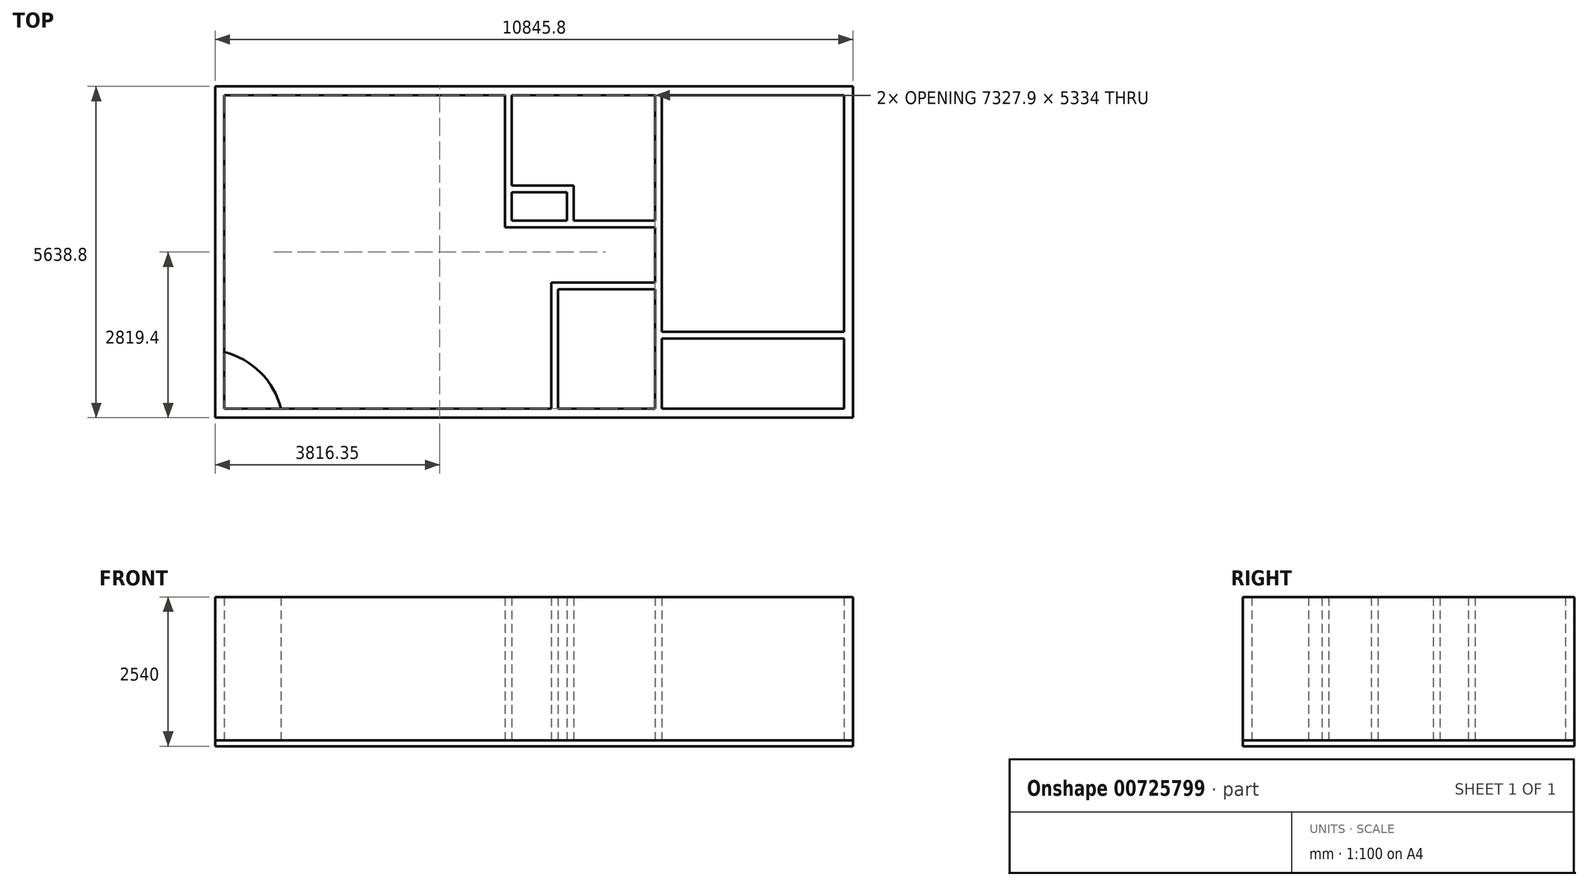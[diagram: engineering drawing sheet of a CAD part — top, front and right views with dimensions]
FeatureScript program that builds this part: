
annotation { "Feature Type Name" : "Feature", "Feature Type Description" : "" }
export const myFeature = defineFeature(function(context is Context, id is Id, definition is map)
    precondition{}
    {
        {
            var Q0;
            Q0=qCreatedBy(makeId("Top.planeOp"),FACE);
            cPlane(context, id + "F0", {"entities" : qUnion([Q0]), "cplaneType" : CPlaneType.OFFSET, "offset" : 1 / 406.4 * mm, "oppositeDirection" : true, "width" : 152.4 * mm, "height" : 152.4 * mm});
        }
        {
            var Q0;
            Q0=qCreatedBy(makeId("Top.planeOp"),FACE);
            var sketch = newSketch(context, id + "F1", { "sketchPlane" : qUnion([Q0])});
            skLineSegment(sketch, "E0.bottom", {"start": v(0, 0) * mm, "end": v(10845.8, 0) * mm});
            skLineSegment(sketch, "E0.top", {"start": v(0, 5638.8) * mm, "end": v(10845.8, 5638.8) * mm});
            skLineSegment(sketch, "E0.left", {"start": v(0, 0) * mm, "end": v(0, 5638.8) * mm});
            skLineSegment(sketch, "E0.right", {"start": v(10845.8, 0) * mm, "end": v(10845.8, 5638.8) * mm});
            skLineSegment(sketch, "E1.0", {"start": v(152.4, 152.4) * mm, "end": v(10693.4, 152.4) * mm, "construction": true});
            skLineSegment(sketch, "E1.1", {"start": v(152.4, 152.4) * mm, "end": v(152.4, 5486.4) * mm, "construction": true});
            skLineSegment(sketch, "E1.2", {"start": v(152.4, 5486.4) * mm, "end": v(10693.4, 5486.4) * mm, "construction": true});
            skLineSegment(sketch, "E1.3", {"start": v(10693.4, 152.4) * mm, "end": v(10693.4, 5486.4) * mm, "construction": true});
            skLineSegment(sketch, "E2.bottom", {"start": v(7480.3, 5486.4) * mm, "end": v(7594.6, 5486.4) * mm, "construction": true});
            skLineSegment(sketch, "E2.top", {"start": v(7480.3, 152.4) * mm, "end": v(7594.6, 152.4) * mm, "construction": true});
            skLineSegment(sketch, "E2.left", {"start": v(7480.3, 5486.4) * mm, "end": v(7480.3, 152.4) * mm, "construction": true});
            skLineSegment(sketch, "E2.right", {"start": v(7594.6, 5486.4) * mm, "end": v(7594.6, 152.4) * mm, "construction": true});
            skLineSegment(sketch, "E3", {"start": v(0, 0) * mm, "end": v(0, -114.3) * mm, "construction": true});
            skLineSegment(sketch, "E4", {"start": v(0, -114.3) * mm, "end": v(-341.18, -114.3) * mm, "construction": true});
            skLineSegment(sketch, "E5", {"start": v(-341.18, -114.3) * mm, "end": v(-341.18, -501.57) * mm, "construction": true});
            skLineSegment(sketch, "E6.bottom", {"start": v(7594.6, 1460.5) * mm, "end": v(10693.4, 1460.5) * mm});
            skLineSegment(sketch, "E6.top", {"start": v(7594.6, 1346.2) * mm, "end": v(10693.4, 1346.2) * mm});
            skLineSegment(sketch, "E6.left", {"start": v(7594.6, 1460.5) * mm, "end": v(7594.6, 1346.2) * mm, "construction": true});
            skLineSegment(sketch, "E6.right", {"start": v(10693.4, 1460.5) * mm, "end": v(10693.4, 1346.2) * mm, "construction": true});
            skLineSegment(sketch, "E7.bottom", {"start": v(4927.6, 5486.4) * mm, "end": v(5041.9, 5486.4) * mm, "construction": true});
            skLineSegment(sketch, "E7.top", {"start": v(4927.6, 3238.5) * mm, "end": v(5041.9, 3238.5) * mm});
            skLineSegment(sketch, "E7.left", {"start": v(4927.6, 5486.4) * mm, "end": v(4927.6, 3238.5) * mm});
            skLineSegment(sketch, "E7.right", {"start": v(5041.9, 5486.4) * mm, "end": v(5041.9, 3238.5) * mm, "construction": true});
            skLineSegment(sketch, "E8.bottom", {"start": v(5041.9, 3238.5) * mm, "end": v(7480.3, 3238.5) * mm});
            skLineSegment(sketch, "E8.top", {"start": v(5041.9, 3352.8) * mm, "end": v(7480.3, 3352.8) * mm, "construction": true});
            skLineSegment(sketch, "E8.left", {"start": v(5041.9, 3238.5) * mm, "end": v(5041.9, 3352.8) * mm, "construction": true});
            skLineSegment(sketch, "E8.right", {"start": v(7480.3, 3238.5) * mm, "end": v(7480.3, 3352.8) * mm, "construction": true});
            skLineSegment(sketch, "E9.bottom", {"start": v(5041.9, 3949.7) * mm, "end": v(6096, 3949.7) * mm});
            skLineSegment(sketch, "E9.top", {"start": v(5041.9, 3835.4) * mm, "end": v(6096, 3835.4) * mm, "construction": true});
            skLineSegment(sketch, "E9.left", {"start": v(5041.9, 3949.7) * mm, "end": v(5041.9, 3835.4) * mm, "construction": true});
            skLineSegment(sketch, "E9.right", {"start": v(6096, 3949.7) * mm, "end": v(6096, 3835.4) * mm});
            skLineSegment(sketch, "E10.bottom", {"start": v(6096, 3835.4) * mm, "end": v(5981.7, 3835.4) * mm, "construction": true});
            skLineSegment(sketch, "E10.top", {"start": v(6096, 3352.8) * mm, "end": v(5981.7, 3352.8) * mm, "construction": true});
            skLineSegment(sketch, "E10.left", {"start": v(6096, 3835.4) * mm, "end": v(6096, 3352.8) * mm});
            skLineSegment(sketch, "E10.right", {"start": v(5981.7, 3835.4) * mm, "end": v(5981.7, 3352.8) * mm});
            skLineSegment(sketch, "E11.bottom", {"start": v(7480.3, 2298.7) * mm, "end": v(5829.3, 2298.7) * mm});
            skLineSegment(sketch, "E11.top", {"start": v(7480.3, 2184.4) * mm, "end": v(5829.3, 2184.4) * mm});
            skLineSegment(sketch, "E11.left", {"start": v(7480.3, 2298.7) * mm, "end": v(7480.3, 2184.4) * mm, "construction": true});
            skLineSegment(sketch, "E11.right", {"start": v(5829.3, 2298.7) * mm, "end": v(5829.3, 2184.4) * mm, "construction": true});
            skLineSegment(sketch, "E12.bottom", {"start": v(5829.3, 2298.7) * mm, "end": v(5715, 2298.7) * mm});
            skLineSegment(sketch, "E12.top", {"start": v(5829.3, 152.4) * mm, "end": v(5715, 152.4) * mm, "construction": true});
            skLineSegment(sketch, "E12.left", {"start": v(5829.3, 2298.7) * mm, "end": v(5829.3, 152.4) * mm, "construction": true});
            skLineSegment(sketch, "E12.right", {"start": v(5715, 2298.7) * mm, "end": v(5715, 152.4) * mm});
            skLineSegment(sketch, "E13", {"start": v(152.4, 5486.4) * mm, "end": v(4927.6, 5486.4) * mm});
            skLineSegment(sketch, "E14", {"start": v(152.4, 5486.4) * mm, "end": v(152.4, 152.4) * mm});
            skLineSegment(sketch, "E15", {"start": v(5715, 152.4) * mm, "end": v(152.4, 152.4) * mm});
            skLineSegment(sketch, "E16", {"start": v(5829.3, 152.4) * mm, "end": v(7480.3, 152.4) * mm});
            skLineSegment(sketch, "E17", {"start": v(7594.6, 152.4) * mm, "end": v(10693.4, 152.4) * mm});
            skLineSegment(sketch, "E18", {"start": v(10693.4, 152.4) * mm, "end": v(10693.4, 1346.2) * mm});
            skLineSegment(sketch, "E19", {"start": v(10693.4, 1460.5) * mm, "end": v(10693.4, 5486.4) * mm});
            skLineSegment(sketch, "E20", {"start": v(10693.4, 5486.4) * mm, "end": v(7594.6, 5486.4) * mm});
            skLineSegment(sketch, "E21", {"start": v(7480.3, 5486.4) * mm, "end": v(5041.9, 5486.4) * mm});
            skLineSegment(sketch, "E22", {"start": v(5041.9, 5486.4) * mm, "end": v(5041.9, 3949.7) * mm});
            skLineSegment(sketch, "E23", {"start": v(5041.9, 3835.4) * mm, "end": v(5041.9, 3352.8) * mm});
            skLineSegment(sketch, "E24", {"start": v(5981.7, 3352.8) * mm, "end": v(5041.9, 3352.8) * mm});
            skLineSegment(sketch, "E25", {"start": v(5981.7, 3835.4) * mm, "end": v(5041.9, 3835.4) * mm});
            skLineSegment(sketch, "E26", {"start": v(6096, 3352.8) * mm, "end": v(7480.3, 3352.8) * mm});
            skLineSegment(sketch, "E27", {"start": v(7480.3, 5486.4) * mm, "end": v(7480.3, 3352.8) * mm});
            skLineSegment(sketch, "E28", {"start": v(7480.3, 3238.5) * mm, "end": v(7480.3, 2298.7) * mm});
            skLineSegment(sketch, "E29", {"start": v(7480.3, 2184.4) * mm, "end": v(7480.3, 152.4) * mm});
            skLineSegment(sketch, "E30", {"start": v(7594.6, 152.4) * mm, "end": v(7594.6, 1346.2) * mm});
            skLineSegment(sketch, "E31", {"start": v(7594.6, 1460.5) * mm, "end": v(7594.6, 5486.4) * mm});
            skLineSegment(sketch, "E32", {"start": v(5829.3, 2184.4) * mm, "end": v(5829.3, 152.4) * mm});
            skSolve(sketch);
        }
        {
            var Q0;
            Q0=qCreatedBy(makeId("Top.planeOp"),FACE);
            var sketch = newSketch(context, id + "F2", { "sketchPlane" : qUnion([Q0])});
            skArc(sketch, "E33", {"start": v(1117.6, 152.4) * mm, "mid": v(769.35, 769.35) * mm, "end": v(152.4, 1117.6) * mm});
            skLineSegment(sketch, "E34", {"start": v(152.4, 1117.6) * mm, "end": v(152.4, 152.4) * mm});
            skLineSegment(sketch, "E35", {"start": v(152.4, 152.4) * mm, "end": v(1117.6, 152.4) * mm});
            skSolve(sketch);
        }
        {
            var Q0;
            Q0 = qSketchRegion(id + "F1", true);
            var Q1;
            Q1 = qSketchRegion(id + "F2", true);
            extrude(context, id + "F3", {"entities" : qUnion([Q0, Q1]), "depth" : 2438.4 * mm, "offsetDistance" : 25.4 * mm});
        }
        {
            var Q0;
            Q0=qCreatedBy(id+"F0.planeOp",FACE);
            var sketch = newSketch(context, id + "F4", { "sketchPlane" : qUnion([Q0])});
            skLineSegment(sketch, "E36.bottom", {"start": v(0, 0) * mm, "end": v(10845.8, 0) * mm});
            skLineSegment(sketch, "E36.top", {"start": v(0, 5638.8) * mm, "end": v(10845.8, 5638.8) * mm});
            skLineSegment(sketch, "E36.left", {"start": v(0, 0) * mm, "end": v(0, 5638.8) * mm});
            skLineSegment(sketch, "E36.right", {"start": v(10845.8, 0) * mm, "end": v(10845.8, 5638.8) * mm});
            skSolve(sketch);
        }
        {
            var Q0;
            Q0 = qSketchRegion(id + "F4", true);
            extrude(context, id + "F5", {"entities" : qUnion([Q0]), "oppositeDirection" : true, "depth" : 101.6 * mm, "offsetDistance" : 25.4 * mm});
        }
    });
